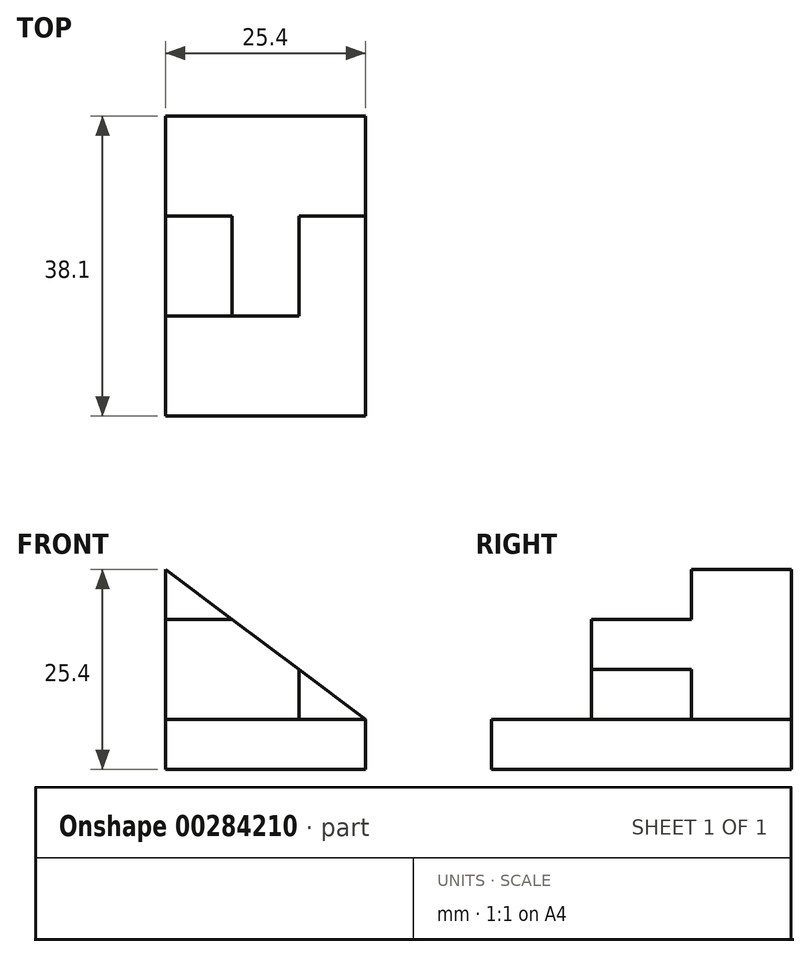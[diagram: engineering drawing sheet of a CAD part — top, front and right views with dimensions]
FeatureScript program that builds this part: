
annotation { "Feature Type Name" : "Feature", "Feature Type Description" : "" }
export const myFeature = defineFeature(function(context is Context, id is Id, definition is map)
    precondition{}
    {
        {
            var Q0;
            Q0=qCreatedBy(makeId("Front.planeOp"),FACE);
            var sketch = newSketch(context, id + "F0", { "sketchPlane" : qUnion([Q0])});
            skLineSegment(sketch, "E0", {"start": v(0, 0) * mm, "end": v(0, 25.4) * mm});
            skLineSegment(sketch, "E1", {"start": v(0, 25.4) * mm, "end": v(25.4, 6.35) * mm});
            skLineSegment(sketch, "E2", {"start": v(25.4, 6.35) * mm, "end": v(25.4, 0) * mm});
            skLineSegment(sketch, "E3", {"start": v(25.4, 0) * mm, "end": v(0, 0) * mm});
            skSolve(sketch);
        }
        {
            var Q0;
            Q0=makeQuery(id+"F0.imprint","IMPRINT",FACE,{"disambiguationData":[TD([[makeQuery(id+"F0.imprint","IMPRINT",EDGE,{"derivedFrom":sQuery(id+"F0.wireOp",EDGE,"E0")}),-1.0]])]});
            extrude(context, id + "F1", {"entities" : qUnion([Q0]), "depth" : 38.1 * mm});
        }
        {
            var Q0;
            Q0=makeQuery(id+"F1.opExtrude","CAP_FACE",FACE,{"disambiguationData":[OSD([sQuery(id+"F0.wireOp",EDGE,"E0"),sQuery(id+"F0.wireOp",EDGE,"E1"),sQuery(id+"F0.wireOp",EDGE,"E2"),sQuery(id+"F0.wireOp",EDGE,"E3")])],"isStart":false});
            var sketch = newSketch(context, id + "F2", { "sketchPlane" : qUnion([Q0])});
            skLineSegment(sketch, "E4", {"start": v(0, 25.4) * mm, "end": v(0, 19.05) * mm});
            skLineSegment(sketch, "E5", {"start": v(0, 19.05) * mm, "end": v(8.47, 19.05) * mm});
            skLineSegment(sketch, "E6", {"start": v(8.47, 19.05) * mm, "end": v(0, 25.4) * mm});
            skLineSegment(sketch, "E7", {"start": v(16.93, 12.7) * mm, "end": v(16.93, 6.35) * mm});
            skLineSegment(sketch, "E8", {"start": v(16.93, 6.35) * mm, "end": v(25.4, 6.35) * mm});
            skLineSegment(sketch, "E9", {"start": v(25.4, 6.35) * mm, "end": v(16.93, 12.7) * mm});
            skLineSegment(sketch, "E10", {"start": v(8.47, 19.05) * mm, "end": v(16.93, 12.7) * mm});
            skLineSegment(sketch, "E11", {"start": v(16.93, 6.35) * mm, "end": v(0, 6.35) * mm});
            skLineSegment(sketch, "E12", {"start": v(0, 6.35) * mm, "end": v(0, 19.05) * mm});
            skSolve(sketch);
        }
        {
            var Q0;
            Q0=makeQuery(id+"F2.imprint","IMPRINT",FACE,{"disambiguationData":[TD([[makeQuery(id+"F2.imprint","IMPRINT",EDGE,{"derivedFrom":sQuery(id+"F2.wireOp",EDGE,"E4")}),-1.0]])]});
            extrude(context, id + "F3", {"entities" : qUnion([Q0]), "operationType" : NewBodyOperationType.REMOVE, "oppositeDirection" : true, "depth" : 25.4 * mm});
        }
        {
            var Q0;
            Q0=makeQuery(id+"F2.imprint","IMPRINT",FACE,{"disambiguationData":[TD([[makeQuery(id+"F2.imprint","IMPRINT",EDGE,{"derivedFrom":sQuery(id+"F2.wireOp",EDGE,"E7")}),1.0]])]});
            extrude(context, id + "F4", {"entities" : qUnion([Q0]), "operationType" : NewBodyOperationType.REMOVE, "oppositeDirection" : true, "depth" : 25.4 * mm});
        }
        {
            var Q0;
            Q0=makeQuery(id+"F2.imprint","IMPRINT",FACE,{"disambiguationData":[TD([[makeQuery(id+"F2.imprint","IMPRINT",EDGE,{"derivedFrom":sQuery(id+"F2.wireOp",EDGE,"E5")}),-1.0]])]});
            extrude(context, id + "F5", {"entities" : qUnion([Q0]), "operationType" : NewBodyOperationType.REMOVE, "oppositeDirection" : true, "depth" : 12.7 * mm});
        }
    });
